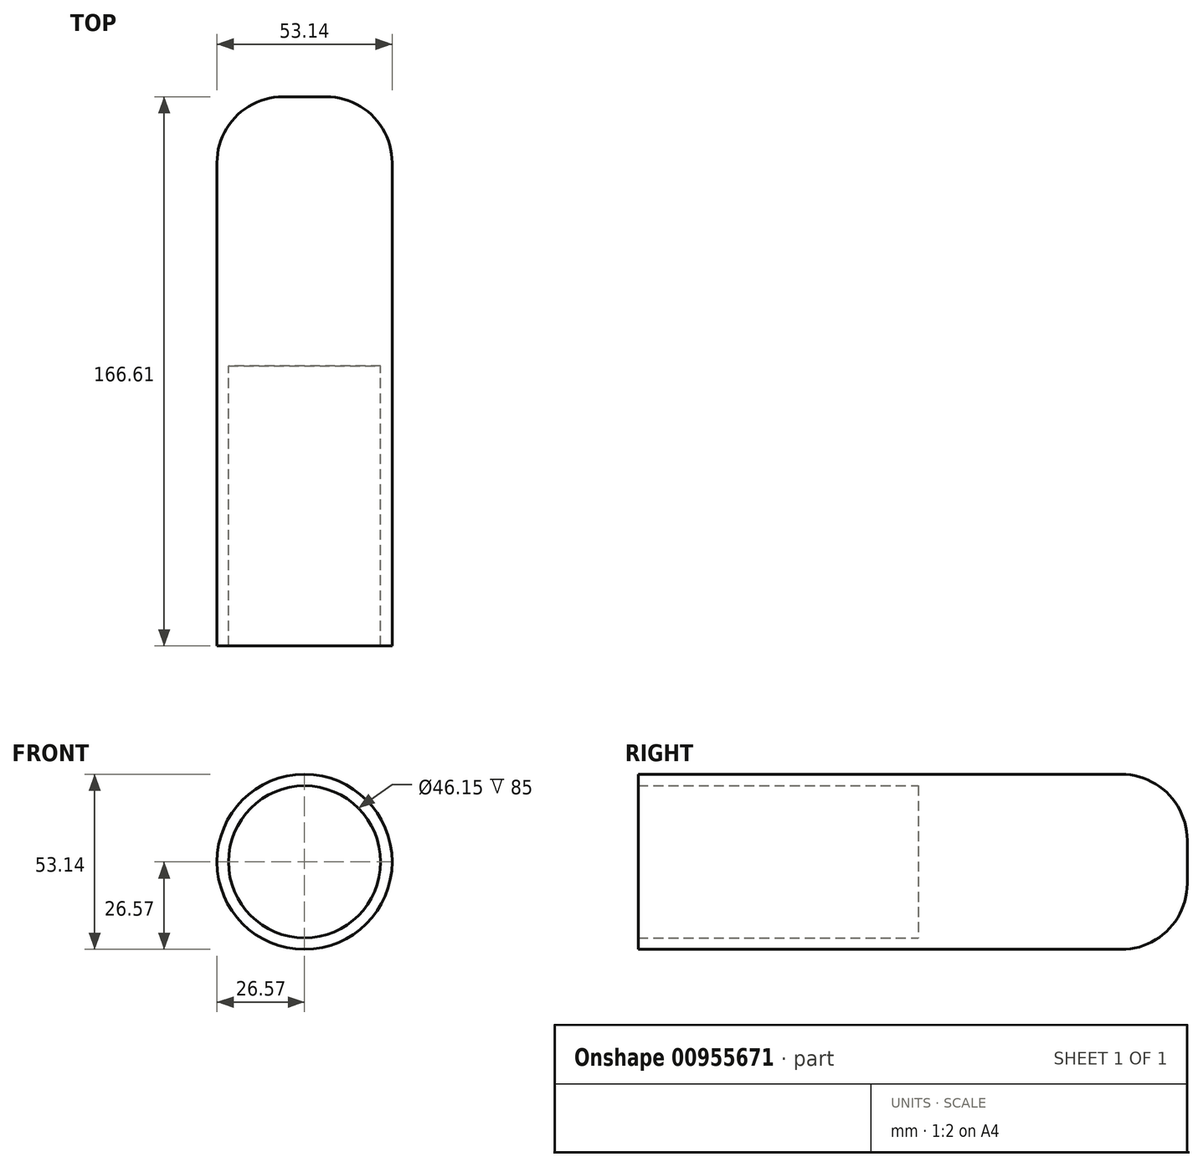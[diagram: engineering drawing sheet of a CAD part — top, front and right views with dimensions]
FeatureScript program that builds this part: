
annotation { "Feature Type Name" : "Feature", "Feature Type Description" : "" }
export const myFeature = defineFeature(function(context is Context, id is Id, definition is map)
    precondition{}
    {
        {
            var Q0;
            Q0=qCreatedBy(makeId("Right.planeOp"),FACE);
            var sketch = newSketch(context, id + "F0", { "sketchPlane" : qUnion([Q0])});
            skLineSegment(sketch, "E0.2", {"start": v(-84.68, 26.57) * mm, "end": v(61.93, 26.57) * mm});
            skLineSegment(sketch, "E1", {"start": v(-84.68, 26.57) * mm, "end": v(-84.68, 23.07) * mm});
            skLineSegment(sketch, "E2", {"start": v(29.6, 0) * mm, "end": v(-42.03, 0) * mm, "construction": true});
            skLineSegment(sketch, "E3", {"start": v(81.93, 6.57) * mm, "end": v(81.93, 0) * mm});
            skLineSegment(sketch, "E4", {"start": v(81.93, 0) * mm, "end": v(0.32, 0) * mm});
            skLineSegment(sketch, "E5", {"start": v(0.32, 0) * mm, "end": v(0.32, 23.07) * mm});
            skLineSegment(sketch, "E6", {"start": v(0.32, 23.07) * mm, "end": v(-84.68, 23.07) * mm});
            skPoint(sketch, "E7.visualSharp", {"position": v(81.93, 26.57) * mm});
            skArc(sketch, "E7.filletArc", {"start": v(81.93, 6.57) * mm, "mid": v(76.07, 20.72) * mm, "end": v(61.93, 26.57) * mm});
            skSolve(sketch);
        }
        {
            var Q0;
            Q0=makeQuery(id+"F0.imprint","IMPRINT",FACE,{"disambiguationData":[TD([[makeQuery(id+"F0.imprint","IMPRINT",EDGE,{"derivedFrom":sQuery(id+"F0.wireOp",EDGE,"E0.2")}),-1.0]])]});
            var Q1;
            Q1=sQuery(id+"F0.wireOp",EDGE,"E2");
            revolve(context, id + "F1", {"surfaceOperationType" : NewSurfaceOperationType.NEW, "entities" : qUnion([Q0]), "axis" : qUnion([Q1]), "revolveType" : RevolveType.FULL});
        }
    });
